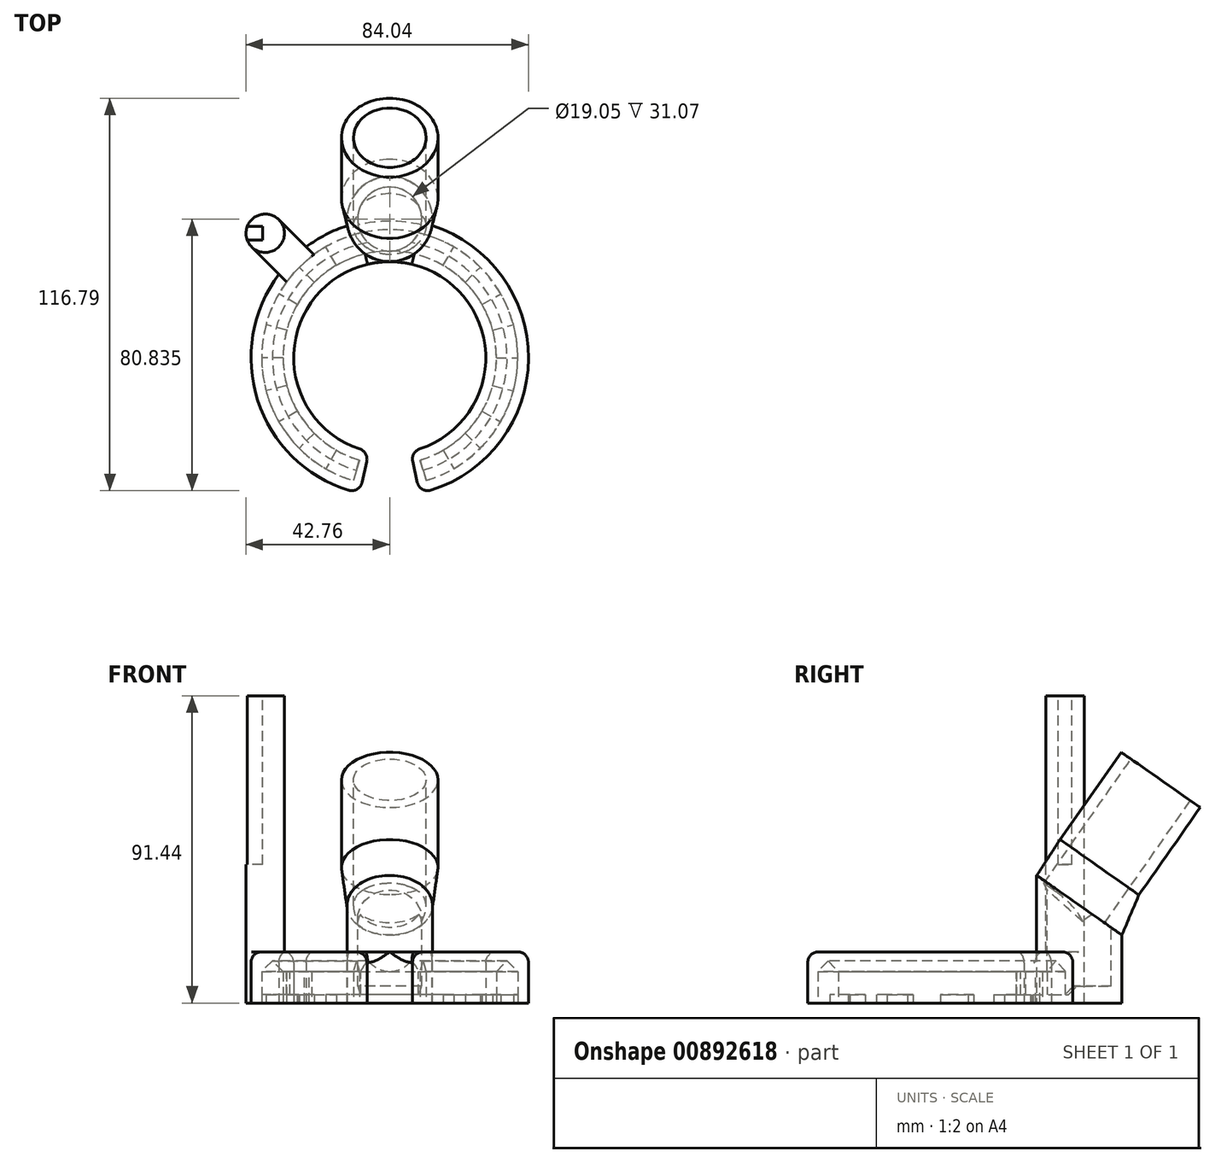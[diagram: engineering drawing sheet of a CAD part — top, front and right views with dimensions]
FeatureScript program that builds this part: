
annotation { "Feature Type Name" : "Feature", "Feature Type Description" : "" }
export const myFeature = defineFeature(function(context is Context, id is Id, definition is map)
    precondition{}
    {
        {
            var Q0;
            Q0=qCreatedBy(makeId("Top.planeOp"),FACE);
            var sketch = newSketch(context, id + "F0", { "sketchPlane" : qUnion([Q0])});
            skCircle(sketch, "E0", {"center": v(0, 0) * mm, "radius": 41.28 * mm});
            skCircle(sketch, "E1", {"center": v(0, 0) * mm, "radius": 28.58 * mm});
            skLineSegment(sketch, "E2", {"start": v(0, 0) * mm, "end": v(-10.13, -45.7) * mm});
            skLineSegment(sketch, "E3", {"start": v(0, 0) * mm, "end": v(10.1, -45.53) * mm});
            skLineSegment(sketch, "E4", {"start": v(0, 0) * mm, "end": v(0, -48.6) * mm});
            skLineSegment(sketch, "E5", {"start": v(0, 0) * mm, "end": v(-13.11, -44.27) * mm});
            skLineSegment(sketch, "E6", {"start": v(0, 0) * mm, "end": v(13.2, -44.55) * mm});
            skCircle(sketch, "E7", {"center": v(0, 0) * mm, "radius": 38.1 * mm, "construction": true});
            skCircle(sketch, "E8", {"center": v(0, 0) * mm, "radius": 31.75 * mm, "construction": true});
            skSolve(sketch);
        }
        {
            var Q0;
            {var subQ0=sQuery(id+"F0.wireOp",EDGE,"E5");var subQ1=sQuery(id+"F0.wireOp",EDGE,"E0");var subQ2=makeQuery(id+"F0.imprint","INTERSECT",VERTEX,{"derivedFrom":[subQ1,subQ0]});Q0=makeQuery(id+"F0.imprint","IMPRINT",FACE,{"disambiguationData":[TD([[makeQuery(id+"F0.imprint","IMPRINT",EDGE,{"disambiguationData":[TD([[subQ2,1.0]])],"derivedFrom":subQ1}),1.0]])]});}
            var Q1;
            {var subQ0=sQuery(id+"F0.wireOp",EDGE,"E5");var subQ1=sQuery(id+"F0.wireOp",EDGE,"E1");var subQ2=makeQuery(id+"F0.imprint","INTERSECT",VERTEX,{"derivedFrom":[subQ1,subQ0]});Q1=makeQuery(id+"F0.imprint","IMPRINT",FACE,{"disambiguationData":[TD([[makeQuery(id+"F0.imprint","IMPRINT",EDGE,{"disambiguationData":[TD([[subQ2,1.0]])],"derivedFrom":subQ1}),-1.0]])]});}
            extrude(context, id + "F1", {"entities" : qUnion([Q0, Q1]), "depth" : 15.24 * mm, "offsetDistance" : 25.4 * mm});
        }
        {
            var Q0;
            Q0=makeQuery(id+"F1.opExtrude","CAP_FACE",FACE,{"disambiguationData":[OSD([sQuery(id+"F0.wireOp",EDGE,"E0"),sQuery(id+"F0.wireOp",EDGE,"E1"),sQuery(id+"F0.wireOp",EDGE,"E5"),sQuery(id+"F0.wireOp",EDGE,"E6")])],"isStart":true});
            var sketch = newSketch(context, id + "F2", { "sketchPlane" : qUnion([Q0])});
            skCircle(sketch, "E9", {"center": v(0, 0) * mm, "radius": 38.1 * mm});
            skCircle(sketch, "E10", {"center": v(0, 0) * mm, "radius": 31.75 * mm});
            skLineSegment(sketch, "E11", {"start": v(0, 0) * mm, "end": v(0, 46.39) * mm});
            skLineSegment(sketch, "E12", {"start": v(0, 0) * mm, "end": v(-12.81, 47.82) * mm});
            skLineSegment(sketch, "E13", {"start": v(0, 0) * mm, "end": v(-48.58, 13.02) * mm});
            skLineSegment(sketch, "E14", {"start": v(0, 0) * mm, "end": v(-52.11, 0) * mm});
            skLineSegment(sketch, "E15", {"start": v(0, 0) * mm, "end": v(-46.55, -12.47) * mm});
            skLineSegment(sketch, "E16", {"start": v(0, 0) * mm, "end": v(-40.24, -23.23) * mm});
            skLineSegment(sketch, "E17", {"start": v(0, 0) * mm, "end": v(11.58, -43.2) * mm});
            skLineSegment(sketch, "E18", {"start": v(0, 0) * mm, "end": v(45.63, 0) * mm});
            skLineSegment(sketch, "E19", {"start": v(0, 0) * mm, "end": v(46.15, 12.37) * mm});
            skLineSegment(sketch, "E20", {"start": v(0, 0) * mm, "end": v(41.38, 23.89) * mm});
            skLineSegment(sketch, "E21", {"start": v(0, 0) * mm, "end": v(36.15, 36.15) * mm});
            skLineSegment(sketch, "E22", {"start": v(0, 0) * mm, "end": v(23.12, 40.04) * mm});
            skLineSegment(sketch, "E23", {"start": v(0, 0) * mm, "end": v(11.24, 41.94) * mm});
            skLineSegment(sketch, "E24", {"start": v(0, 0) * mm, "end": v(-24.22, 41.95) * mm});
            skLineSegment(sketch, "E25", {"start": v(0, 0) * mm, "end": v(-32.47, 32.47) * mm});
            skLineSegment(sketch, "E26", {"start": v(0, 0) * mm, "end": v(-45.6, 26.33) * mm});
            skLineSegment(sketch, "E27", {"start": v(0, 0) * mm, "end": v(-33.36, -33.36) * mm});
            skLineSegment(sketch, "E28", {"start": v(0, 0) * mm, "end": v(-22.54, -39.05) * mm});
            skLineSegment(sketch, "E29", {"start": v(0, 0) * mm, "end": v(-11.37, -42.45) * mm});
            skLineSegment(sketch, "E30", {"start": v(0, 0) * mm, "end": v(45.05, -12.07) * mm});
            skLineSegment(sketch, "E31", {"start": v(0, 0) * mm, "end": v(42.5, -24.54) * mm});
            skLineSegment(sketch, "E32", {"start": v(0, 0) * mm, "end": v(33.86, -33.86) * mm});
            skLineSegment(sketch, "E33", {"start": v(0, 0) * mm, "end": v(23.17, -40.14) * mm});
            skLineSegment(sketch, "E34", {"start": v(0, 0) * mm, "end": v(0, -46.71) * mm});
            skSolve(sketch);
        }
        {
            var Q0;
            {var subQ0=sQuery(id+"F2.wireOp",EDGE,"E24");var subQ1=sQuery(id+"F2.wireOp",EDGE,"E9");var subQ2=makeQuery(id+"F2.imprint","INTERSECT",VERTEX,{"derivedFrom":[subQ1,subQ0]});Q0=makeQuery(id+"F2.imprint","IMPRINT",FACE,{"disambiguationData":[TD([[makeQuery(id+"F2.imprint","IMPRINT",EDGE,{"disambiguationData":[TD([[subQ2,1.0]])],"derivedFrom":subQ1}),1.0]])]});}
            var Q1;
            {var subQ0=sQuery(id+"F2.wireOp",EDGE,"E25");var subQ1=sQuery(id+"F2.wireOp",EDGE,"E9");var subQ2=makeQuery(id+"F2.imprint","INTERSECT",VERTEX,{"derivedFrom":[subQ1,subQ0]});Q1=makeQuery(id+"F2.imprint","IMPRINT",FACE,{"disambiguationData":[TD([[makeQuery(id+"F2.imprint","IMPRINT",EDGE,{"disambiguationData":[TD([[subQ2,-1.0]])],"derivedFrom":subQ1}),1.0]])]});}
            var Q2;
            {var subQ0=sQuery(id+"F2.wireOp",EDGE,"E13");var subQ1=sQuery(id+"F2.wireOp",EDGE,"E9");var subQ2=makeQuery(id+"F2.imprint","INTERSECT",VERTEX,{"derivedFrom":[subQ1,subQ0]});Q2=makeQuery(id+"F2.imprint","IMPRINT",FACE,{"disambiguationData":[TD([[makeQuery(id+"F2.imprint","IMPRINT",EDGE,{"disambiguationData":[TD([[subQ2,-1.0]])],"derivedFrom":subQ1}),1.0]])]});}
            var Q3;
            {var subQ0=sQuery(id+"F2.wireOp",EDGE,"E15");var subQ1=sQuery(id+"F2.wireOp",EDGE,"E9");var subQ2=makeQuery(id+"F2.imprint","INTERSECT",VERTEX,{"derivedFrom":[subQ1,subQ0]});Q3=makeQuery(id+"F2.imprint","IMPRINT",FACE,{"disambiguationData":[TD([[makeQuery(id+"F2.imprint","IMPRINT",EDGE,{"disambiguationData":[TD([[subQ2,-1.0]])],"derivedFrom":subQ1}),1.0]])]});}
            var Q4;
            {var subQ0=sQuery(id+"F2.wireOp",EDGE,"E27");var subQ1=sQuery(id+"F2.wireOp",EDGE,"E9");var subQ2=makeQuery(id+"F2.imprint","INTERSECT",VERTEX,{"derivedFrom":[subQ1,subQ0]});Q4=makeQuery(id+"F2.imprint","IMPRINT",FACE,{"disambiguationData":[TD([[makeQuery(id+"F2.imprint","IMPRINT",EDGE,{"disambiguationData":[TD([[subQ2,-1.0]])],"derivedFrom":subQ1}),1.0]])]});}
            var Q5;
            {var subQ0=sQuery(id+"F2.wireOp",EDGE,"E22");var subQ1=sQuery(id+"F2.wireOp",EDGE,"E9");var subQ2=makeQuery(id+"F2.imprint","INTERSECT",VERTEX,{"derivedFrom":[subQ1,subQ0]});Q5=makeQuery(id+"F2.imprint","IMPRINT",FACE,{"disambiguationData":[TD([[makeQuery(id+"F2.imprint","IMPRINT",EDGE,{"disambiguationData":[TD([[subQ2,-1.0]])],"derivedFrom":subQ1}),1.0]])]});}
            var Q6;
            {var subQ0=sQuery(id+"F2.wireOp",EDGE,"E20");var subQ1=sQuery(id+"F2.wireOp",EDGE,"E9");var subQ2=makeQuery(id+"F2.imprint","INTERSECT",VERTEX,{"derivedFrom":[subQ1,subQ0]});Q6=makeQuery(id+"F2.imprint","IMPRINT",FACE,{"disambiguationData":[TD([[makeQuery(id+"F2.imprint","IMPRINT",EDGE,{"disambiguationData":[TD([[subQ2,-1.0]])],"derivedFrom":subQ1}),1.0]])]});}
            var Q7;
            {var subQ0=sQuery(id+"F2.wireOp",EDGE,"E19");var subQ1=sQuery(id+"F2.wireOp",EDGE,"E9");var subQ2=makeQuery(id+"F2.imprint","INTERSECT",VERTEX,{"derivedFrom":[subQ1,subQ0]});Q7=makeQuery(id+"F2.imprint","IMPRINT",FACE,{"disambiguationData":[TD([[makeQuery(id+"F2.imprint","IMPRINT",EDGE,{"disambiguationData":[TD([[subQ2,1.0]])],"derivedFrom":subQ1}),1.0]])]});}
            var Q8;
            {var subQ0=sQuery(id+"F2.wireOp",EDGE,"E31");var subQ1=sQuery(id+"F2.wireOp",EDGE,"E9");var subQ2=makeQuery(id+"F2.imprint","INTERSECT",VERTEX,{"derivedFrom":[subQ1,subQ0]});Q8=makeQuery(id+"F2.imprint","IMPRINT",FACE,{"disambiguationData":[TD([[makeQuery(id+"F2.imprint","IMPRINT",EDGE,{"disambiguationData":[TD([[subQ2,-1.0]])],"derivedFrom":subQ1}),1.0]])]});}
            var Q9;
            {var subQ0=sQuery(id+"F2.wireOp",EDGE,"E33");var subQ1=sQuery(id+"F2.wireOp",EDGE,"E9");var subQ2=makeQuery(id+"F2.imprint","INTERSECT",VERTEX,{"derivedFrom":[subQ1,subQ0]});Q9=makeQuery(id+"F2.imprint","IMPRINT",FACE,{"disambiguationData":[TD([[makeQuery(id+"F2.imprint","IMPRINT",EDGE,{"disambiguationData":[TD([[subQ2,-1.0]])],"derivedFrom":subQ1}),1.0]])]});}
            extrude(context, id + "F3", {"entities" : qUnion([Q0, Q1, Q2, Q3, Q4, Q5, Q6, Q7, Q8, Q9]), "operationType" : NewBodyOperationType.REMOVE, "oppositeDirection" : true, "depth" : 12.7 * mm, "offsetDistance" : 25.4 * mm});
        }
        {
            var Q0;
            Q0=makeQuery(id+"F1.opExtrude","SWEPT_FACE",FACE,{"disambiguationData":[OSD([sQuery(id+"F0.wireOp",EDGE,"E5")])]});
            var sketch = newSketch(context, id + "F4", { "sketchPlane" : qUnion([Q0])});
            skLineSegment(sketch, "E35.bottom", {"start": v(-31.75, 12.7) * mm, "end": v(-38.1, 12.7) * mm});
            skLineSegment(sketch, "E35.top", {"start": v(-31.75, 2.54) * mm, "end": v(-38.1, 2.54) * mm});
            skLineSegment(sketch, "E35.left", {"start": v(-31.75, 12.7) * mm, "end": v(-31.75, 2.54) * mm});
            skLineSegment(sketch, "E35.right", {"start": v(-38.1, 12.7) * mm, "end": v(-38.1, 2.54) * mm});
            skLineSegment(sketch, "E36", {"start": v(0, 0) * mm, "end": v(0, 28.6) * mm});
            skSolve(sketch);
        }
        {
            var Q0;
            Q0=makeQuery(id+"F4.imprint","IMPRINT",FACE,{"disambiguationData":[TD([[makeQuery(id+"F4.imprint","IMPRINT",EDGE,{"derivedFrom":sQuery(id+"F4.wireOp",EDGE,"E35.bottom")}),1.0]])]});
            var Q1;
            Q1=sQuery(id+"F4.wireOp",EDGE,"E36");
            revolve(context, id + "F5", {"operationType" : NewBodyOperationType.REMOVE, "surfaceOperationType" : NewSurfaceOperationType.NEW, "entities" : qUnion([Q0]), "axis" : qUnion([Q1]), "revolveType" : RevolveType.FULL, "oppositeDirection" : true});
        }
        {
            var Q0;
            {var subQ0=sQuery(id+"F0.wireOp",EDGE,"E2");var subQ1=sQuery(id+"F0.wireOp",EDGE,"E0");var subQ2=makeQuery(id+"F0.imprint","INTERSECT",VERTEX,{"derivedFrom":[subQ1,subQ0]});Q0=makeQuery(id+"F0.imprint","IMPRINT",FACE,{"disambiguationData":[TD([[makeQuery(id+"F0.imprint","IMPRINT",EDGE,{"disambiguationData":[TD([[subQ2,1.0]])],"derivedFrom":subQ1}),1.0]])]});}
            var Q1;
            {var subQ0=sQuery(id+"F0.wireOp",EDGE,"E3");var subQ1=sQuery(id+"F0.wireOp",EDGE,"E0");var subQ2=makeQuery(id+"F0.imprint","INTERSECT",VERTEX,{"derivedFrom":[subQ1,subQ0]});Q1=makeQuery(id+"F0.imprint","IMPRINT",FACE,{"disambiguationData":[TD([[makeQuery(id+"F0.imprint","IMPRINT",EDGE,{"disambiguationData":[TD([[subQ2,-1.0]])],"derivedFrom":subQ1}),1.0]])]});}
            extrude(context, id + "F6", {"entities" : qUnion([Q0, Q1]), "operationType" : NewBodyOperationType.ADD, "depth" : 15.24 * mm, "offsetDistance" : 25.4 * mm});
        }
        {
            var Q0;
            {var subQ0=sQuery(id+"F2.wireOp",EDGE,"E10");Q0=makeQuery(id+"F5.boolean.opBoolean","MERGE",EDGE,{"derivedFrom":[makeQuery(id+"F3.boolean.opBoolean","COPY",EDGE,{"derivedFrom":makeQuery(id+"F3.opExtrude","CAP_EDGE",EDGE,{"disambiguationData":[OSD([subQ0]),TDD([makeQuery(id+"F2.imprint","IMPRINT",EDGE,{"disambiguationData":[TD([[makeQuery(id+"F2.imprint","INTERSECT",VERTEX,{"derivedFrom":[subQ0,sQuery(id+"F2.wireOp",EDGE,"E19")]}),1.0]])],"derivedFrom":subQ0})])],"isStart":false})}),makeQuery(id+"F3.boolean.opBoolean","COPY",EDGE,{"derivedFrom":makeQuery(id+"F3.opExtrude","CAP_EDGE",EDGE,{"disambiguationData":[OSD([subQ0]),TDD([makeQuery(id+"F2.imprint","IMPRINT",EDGE,{"disambiguationData":[TD([[makeQuery(id+"F2.imprint","INTERSECT",VERTEX,{"derivedFrom":[subQ0,sQuery(id+"F2.wireOp",EDGE,"E20")]}),-1.0]])],"derivedFrom":subQ0})])],"isStart":false})}),makeQuery(id+"F3.boolean.opBoolean","COPY",EDGE,{"derivedFrom":makeQuery(id+"F3.opExtrude","CAP_EDGE",EDGE,{"disambiguationData":[OSD([subQ0]),TDD([makeQuery(id+"F2.imprint","IMPRINT",EDGE,{"disambiguationData":[TD([[makeQuery(id+"F2.imprint","INTERSECT",VERTEX,{"derivedFrom":[subQ0,sQuery(id+"F2.wireOp",EDGE,"E22")]}),-1.0]])],"derivedFrom":subQ0})])],"isStart":false})}),makeQuery(id+"F3.boolean.opBoolean","COPY",EDGE,{"derivedFrom":makeQuery(id+"F3.opExtrude","CAP_EDGE",EDGE,{"disambiguationData":[OSD([subQ0]),TDD([makeQuery(id+"F2.imprint","IMPRINT",EDGE,{"disambiguationData":[TD([[makeQuery(id+"F2.imprint","INTERSECT",VERTEX,{"derivedFrom":[subQ0,sQuery(id+"F2.wireOp",EDGE,"E24")]}),1.0]])],"derivedFrom":subQ0})])],"isStart":false})}),makeQuery(id+"F3.boolean.opBoolean","COPY",EDGE,{"derivedFrom":makeQuery(id+"F3.opExtrude","CAP_EDGE",EDGE,{"disambiguationData":[OSD([subQ0]),TDD([makeQuery(id+"F2.imprint","IMPRINT",EDGE,{"disambiguationData":[TD([[makeQuery(id+"F2.imprint","INTERSECT",VERTEX,{"derivedFrom":[subQ0,sQuery(id+"F2.wireOp",EDGE,"E25")]}),-1.0]])],"derivedFrom":subQ0})])],"isStart":false})}),makeQuery(id+"F3.boolean.opBoolean","COPY",EDGE,{"derivedFrom":makeQuery(id+"F3.opExtrude","CAP_EDGE",EDGE,{"disambiguationData":[OSD([subQ0]),TDD([makeQuery(id+"F2.imprint","IMPRINT",EDGE,{"disambiguationData":[TD([[makeQuery(id+"F2.imprint","INTERSECT",VERTEX,{"derivedFrom":[subQ0,sQuery(id+"F2.wireOp",EDGE,"E13")]}),-1.0]])],"derivedFrom":subQ0})])],"isStart":false})}),makeQuery(id+"F3.boolean.opBoolean","COPY",EDGE,{"derivedFrom":makeQuery(id+"F3.opExtrude","CAP_EDGE",EDGE,{"disambiguationData":[OSD([subQ0]),TDD([makeQuery(id+"F2.imprint","IMPRINT",EDGE,{"disambiguationData":[TD([[makeQuery(id+"F2.imprint","INTERSECT",VERTEX,{"derivedFrom":[subQ0,sQuery(id+"F2.wireOp",EDGE,"E15")]}),-1.0]])],"derivedFrom":subQ0})])],"isStart":false})}),makeQuery(id+"F3.boolean.opBoolean","COPY",EDGE,{"derivedFrom":makeQuery(id+"F3.opExtrude","CAP_EDGE",EDGE,{"disambiguationData":[OSD([subQ0]),TDD([makeQuery(id+"F2.imprint","IMPRINT",EDGE,{"disambiguationData":[TD([[makeQuery(id+"F2.imprint","INTERSECT",VERTEX,{"derivedFrom":[subQ0,sQuery(id+"F2.wireOp",EDGE,"E27")]}),-1.0]])],"derivedFrom":subQ0})])],"isStart":false})}),makeQuery(id+"F3.boolean.opBoolean","COPY",EDGE,{"derivedFrom":makeQuery(id+"F3.opExtrude","CAP_EDGE",EDGE,{"disambiguationData":[OSD([subQ0]),TDD([makeQuery(id+"F2.imprint","IMPRINT",EDGE,{"disambiguationData":[TD([[makeQuery(id+"F2.imprint","INTERSECT",VERTEX,{"derivedFrom":[subQ0,sQuery(id+"F2.wireOp",EDGE,"E29")]}),-1.0]])],"derivedFrom":subQ0})])],"isStart":false})}),makeQuery(id+"F3.boolean.opBoolean","COPY",EDGE,{"derivedFrom":makeQuery(id+"F3.opExtrude","CAP_EDGE",EDGE,{"disambiguationData":[OSD([subQ0]),TDD([makeQuery(id+"F2.imprint","IMPRINT",EDGE,{"disambiguationData":[TD([[makeQuery(id+"F2.imprint","INTERSECT",VERTEX,{"derivedFrom":[subQ0,sQuery(id+"F2.wireOp",EDGE,"E33")]}),-1.0]])],"derivedFrom":subQ0})])],"isStart":false})}),makeQuery(id+"F3.boolean.opBoolean","COPY",EDGE,{"derivedFrom":makeQuery(id+"F3.opExtrude","CAP_EDGE",EDGE,{"disambiguationData":[OSD([subQ0]),TDD([makeQuery(id+"F2.imprint","IMPRINT",EDGE,{"disambiguationData":[TD([[makeQuery(id+"F2.imprint","INTERSECT",VERTEX,{"derivedFrom":[subQ0,sQuery(id+"F2.wireOp",EDGE,"E31")]}),-1.0]])],"derivedFrom":subQ0})])],"isStart":false})})],"fromTools":[makeQuery(id+"F5.opRevolve","SWEPT_EDGE",EDGE,{"disambiguationData":[OSD([sQuery(id+"F4.wireOp",EDGE,"E35.bottom"),sQuery(id+"F4.wireOp",EDGE,"E35.left")])]})]});}
            var Q1;
            {var subQ0=sQuery(id+"F2.wireOp",EDGE,"E9");Q1=makeQuery(id+"F5.boolean.opBoolean","MERGE",EDGE,{"derivedFrom":[makeQuery(id+"F3.boolean.opBoolean","COPY",EDGE,{"derivedFrom":makeQuery(id+"F3.opExtrude","CAP_EDGE",EDGE,{"disambiguationData":[OSD([subQ0]),TDD([makeQuery(id+"F2.imprint","IMPRINT",EDGE,{"disambiguationData":[TD([[makeQuery(id+"F2.imprint","INTERSECT",VERTEX,{"derivedFrom":[subQ0,sQuery(id+"F2.wireOp",EDGE,"E19")]}),1.0]])],"derivedFrom":subQ0})])],"isStart":false})}),makeQuery(id+"F3.boolean.opBoolean","COPY",EDGE,{"derivedFrom":makeQuery(id+"F3.opExtrude","CAP_EDGE",EDGE,{"disambiguationData":[OSD([subQ0]),TDD([makeQuery(id+"F2.imprint","IMPRINT",EDGE,{"disambiguationData":[TD([[makeQuery(id+"F2.imprint","INTERSECT",VERTEX,{"derivedFrom":[subQ0,sQuery(id+"F2.wireOp",EDGE,"E20")]}),-1.0]])],"derivedFrom":subQ0})])],"isStart":false})}),makeQuery(id+"F3.boolean.opBoolean","COPY",EDGE,{"derivedFrom":makeQuery(id+"F3.opExtrude","CAP_EDGE",EDGE,{"disambiguationData":[OSD([subQ0]),TDD([makeQuery(id+"F2.imprint","IMPRINT",EDGE,{"disambiguationData":[TD([[makeQuery(id+"F2.imprint","INTERSECT",VERTEX,{"derivedFrom":[subQ0,sQuery(id+"F2.wireOp",EDGE,"E22")]}),-1.0]])],"derivedFrom":subQ0})])],"isStart":false})}),makeQuery(id+"F3.boolean.opBoolean","COPY",EDGE,{"derivedFrom":makeQuery(id+"F3.opExtrude","CAP_EDGE",EDGE,{"disambiguationData":[OSD([subQ0]),TDD([makeQuery(id+"F2.imprint","IMPRINT",EDGE,{"disambiguationData":[TD([[makeQuery(id+"F2.imprint","INTERSECT",VERTEX,{"derivedFrom":[subQ0,sQuery(id+"F2.wireOp",EDGE,"E24")]}),1.0]])],"derivedFrom":subQ0})])],"isStart":false})}),makeQuery(id+"F3.boolean.opBoolean","COPY",EDGE,{"derivedFrom":makeQuery(id+"F3.opExtrude","CAP_EDGE",EDGE,{"disambiguationData":[OSD([subQ0]),TDD([makeQuery(id+"F2.imprint","IMPRINT",EDGE,{"disambiguationData":[TD([[makeQuery(id+"F2.imprint","INTERSECT",VERTEX,{"derivedFrom":[subQ0,sQuery(id+"F2.wireOp",EDGE,"E25")]}),-1.0]])],"derivedFrom":subQ0})])],"isStart":false})}),makeQuery(id+"F3.boolean.opBoolean","COPY",EDGE,{"derivedFrom":makeQuery(id+"F3.opExtrude","CAP_EDGE",EDGE,{"disambiguationData":[OSD([subQ0]),TDD([makeQuery(id+"F2.imprint","IMPRINT",EDGE,{"disambiguationData":[TD([[makeQuery(id+"F2.imprint","INTERSECT",VERTEX,{"derivedFrom":[subQ0,sQuery(id+"F2.wireOp",EDGE,"E13")]}),-1.0]])],"derivedFrom":subQ0})])],"isStart":false})}),makeQuery(id+"F3.boolean.opBoolean","COPY",EDGE,{"derivedFrom":makeQuery(id+"F3.opExtrude","CAP_EDGE",EDGE,{"disambiguationData":[OSD([subQ0]),TDD([makeQuery(id+"F2.imprint","IMPRINT",EDGE,{"disambiguationData":[TD([[makeQuery(id+"F2.imprint","INTERSECT",VERTEX,{"derivedFrom":[subQ0,sQuery(id+"F2.wireOp",EDGE,"E15")]}),-1.0]])],"derivedFrom":subQ0})])],"isStart":false})}),makeQuery(id+"F3.boolean.opBoolean","COPY",EDGE,{"derivedFrom":makeQuery(id+"F3.opExtrude","CAP_EDGE",EDGE,{"disambiguationData":[OSD([subQ0]),TDD([makeQuery(id+"F2.imprint","IMPRINT",EDGE,{"disambiguationData":[TD([[makeQuery(id+"F2.imprint","INTERSECT",VERTEX,{"derivedFrom":[subQ0,sQuery(id+"F2.wireOp",EDGE,"E27")]}),-1.0]])],"derivedFrom":subQ0})])],"isStart":false})}),makeQuery(id+"F3.boolean.opBoolean","COPY",EDGE,{"derivedFrom":makeQuery(id+"F3.opExtrude","CAP_EDGE",EDGE,{"disambiguationData":[OSD([subQ0]),TDD([makeQuery(id+"F2.imprint","IMPRINT",EDGE,{"disambiguationData":[TD([[makeQuery(id+"F2.imprint","INTERSECT",VERTEX,{"derivedFrom":[subQ0,sQuery(id+"F2.wireOp",EDGE,"E29")]}),-1.0]])],"derivedFrom":subQ0})])],"isStart":false})}),makeQuery(id+"F3.boolean.opBoolean","COPY",EDGE,{"derivedFrom":makeQuery(id+"F3.opExtrude","CAP_EDGE",EDGE,{"disambiguationData":[OSD([subQ0]),TDD([makeQuery(id+"F2.imprint","IMPRINT",EDGE,{"disambiguationData":[TD([[makeQuery(id+"F2.imprint","INTERSECT",VERTEX,{"derivedFrom":[subQ0,sQuery(id+"F2.wireOp",EDGE,"E33")]}),-1.0]])],"derivedFrom":subQ0})])],"isStart":false})}),makeQuery(id+"F3.boolean.opBoolean","COPY",EDGE,{"derivedFrom":makeQuery(id+"F3.opExtrude","CAP_EDGE",EDGE,{"disambiguationData":[OSD([subQ0]),TDD([makeQuery(id+"F2.imprint","IMPRINT",EDGE,{"disambiguationData":[TD([[makeQuery(id+"F2.imprint","INTERSECT",VERTEX,{"derivedFrom":[subQ0,sQuery(id+"F2.wireOp",EDGE,"E31")]}),-1.0]])],"derivedFrom":subQ0})])],"isStart":false})})],"fromTools":[makeQuery(id+"F5.opRevolve","SWEPT_EDGE",EDGE,{"disambiguationData":[OSD([sQuery(id+"F4.wireOp",EDGE,"E35.bottom"),sQuery(id+"F4.wireOp",EDGE,"E35.right")])]})]});}
            chamfer(context, id + "F7", {"entities" : qUnion([Q0, Q1]), "width" : 3.3 * mm, "tangentPropagation" : true});
        }
        {
            var Q0;
            {var subQ0=sQuery(id+"F0.wireOp",EDGE,"E6");var subQ1=sQuery(id+"F0.wireOp",EDGE,"E1");var subQ2=sQuery(id+"F0.wireOp",EDGE,"E0");var subQ3=sQuery(id+"F0.wireOp",EDGE,"E5");Q0=makeQuery(id+"F6.boolean.opBoolean","MERGE",FACE,{"derivedFrom":[makeQuery(id+"F1.opExtrude","CAP_FACE",FACE,{"disambiguationData":[OSD([subQ2,subQ1,subQ3,subQ0])],"isStart":false}),makeQuery(id+"F6.opExtrude","CAP_FACE",FACE,{"disambiguationData":[OSD([subQ2,subQ1,sQuery(id+"F0.wireOp",EDGE,"E2"),subQ3])],"isStart":false}),makeQuery(id+"F6.opExtrude","CAP_FACE",FACE,{"disambiguationData":[OSD([subQ2,subQ1,sQuery(id+"F0.wireOp",EDGE,"E3"),subQ0])],"isStart":false})]});}
            var sketch = newSketch(context, id + "F8", { "sketchPlane" : qUnion([Q0])});
            skCircle(sketch, "E37", {"center": v(0, 41.28) * mm, "radius": 12.7 * mm});
            skCircle(sketch, "E38", {"center": v(0, 41.28) * mm, "radius": 9.53 * mm});
            skSolve(sketch);
        }
        {
            var Q0;
            {var subQ0=sQuery(id+"F8.wireOp",EDGE,"E37");var subQ1=sQuery(id+"F0.wireOp",EDGE,"E0");var subQ2=makeQuery(id+"F6.boolean.opBoolean","MERGE",EDGE,{"derivedFrom":[makeQuery(id+"F1.opExtrude","CAP_EDGE",EDGE,{"disambiguationData":[OSD([subQ1])],"isStart":false}),makeQuery(id+"F6.opExtrude","CAP_EDGE",EDGE,{"disambiguationData":[OSD([subQ1]),TDD([makeQuery(id+"F0.imprint","IMPRINT",EDGE,{"disambiguationData":[TD([[makeQuery(id+"F0.imprint","INTERSECT",VERTEX,{"derivedFrom":[subQ1,sQuery(id+"F0.wireOp",EDGE,"E2")]}),1.0]])],"derivedFrom":subQ1})])],"isStart":false}),makeQuery(id+"F6.opExtrude","CAP_EDGE",EDGE,{"disambiguationData":[OSD([subQ1]),TDD([makeQuery(id+"F0.imprint","IMPRINT",EDGE,{"disambiguationData":[TD([[makeQuery(id+"F0.imprint","INTERSECT",VERTEX,{"derivedFrom":[subQ1,sQuery(id+"F0.wireOp",EDGE,"E3")]}),-1.0]])],"derivedFrom":subQ1})])],"isStart":false})]});var subQ3=makeQuery(id+"F8.imprint","INTERSECT",VERTEX,{"disambiguationData":[OD(0.0)],"derivedFrom":[subQ2,subQ0]});Q0=makeQuery(id+"F8.imprint","IMPRINT",FACE,{"disambiguationData":[TD([[makeQuery(id+"F8.imprint","IMPRINT",EDGE,{"disambiguationData":[TD([[subQ3,1.0]])],"derivedFrom":subQ0}),1.0]])]});}
            extrude(context, id + "F9", {"entities" : qUnion([Q0]), "operationType" : NewBodyOperationType.ADD, "oppositeDirection" : true, "depth" : 15.24 * mm, "offsetDistance" : 25.4 * mm});
        }
        {
            var Q0;
            {var subQ1=sQuery(id+"F0.wireOp",EDGE,"E3");var subQ4=sQuery(id+"F0.wireOp",EDGE,"E2");var subQ9=sQuery(id+"F8.wireOp",EDGE,"E37");var subQ11=sQuery(id+"F0.wireOp",EDGE,"E1");var subQ12=makeQuery(id+"F8.imprint","INTERSECT",VERTEX,{"derivedFrom":[makeQuery(id+"F6.boolean.opBoolean","MERGE",EDGE,{"derivedFrom":[makeQuery(id+"F1.opExtrude","CAP_EDGE",EDGE,{"disambiguationData":[OSD([subQ11])],"isStart":false}),makeQuery(id+"F6.opExtrude","CAP_EDGE",EDGE,{"disambiguationData":[OSD([subQ11]),TDD([makeQuery(id+"F0.imprint","IMPRINT",EDGE,{"disambiguationData":[TD([[makeQuery(id+"F0.imprint","INTERSECT",VERTEX,{"derivedFrom":[subQ11,subQ4]}),1.0]])],"derivedFrom":subQ11})])],"isStart":false}),makeQuery(id+"F6.opExtrude","CAP_EDGE",EDGE,{"disambiguationData":[OSD([subQ11]),TDD([makeQuery(id+"F0.imprint","IMPRINT",EDGE,{"disambiguationData":[TD([[makeQuery(id+"F0.imprint","INTERSECT",VERTEX,{"derivedFrom":[subQ11,subQ1]}),-1.0]])],"derivedFrom":subQ11})])],"isStart":false})]}),subQ9]});Q0=makeQuery(id+"F8.imprint","IMPRINT",FACE,{"disambiguationData":[TD([[makeQuery(id+"F8.imprint","IMPRINT",EDGE,{"disambiguationData":[TD([[subQ12,1.0]])],"derivedFrom":subQ9}),1.0]])]});}
            var Q1;
            {var subQ0=sQuery(id+"F8.wireOp",EDGE,"E37");var subQ1=sQuery(id+"F0.wireOp",EDGE,"E0");var subQ2=makeQuery(id+"F6.boolean.opBoolean","MERGE",EDGE,{"derivedFrom":[makeQuery(id+"F1.opExtrude","CAP_EDGE",EDGE,{"disambiguationData":[OSD([subQ1])],"isStart":false}),makeQuery(id+"F6.opExtrude","CAP_EDGE",EDGE,{"disambiguationData":[OSD([subQ1]),TDD([makeQuery(id+"F0.imprint","IMPRINT",EDGE,{"disambiguationData":[TD([[makeQuery(id+"F0.imprint","INTERSECT",VERTEX,{"derivedFrom":[subQ1,sQuery(id+"F0.wireOp",EDGE,"E2")]}),1.0]])],"derivedFrom":subQ1})])],"isStart":false}),makeQuery(id+"F6.opExtrude","CAP_EDGE",EDGE,{"disambiguationData":[OSD([subQ1]),TDD([makeQuery(id+"F0.imprint","IMPRINT",EDGE,{"disambiguationData":[TD([[makeQuery(id+"F0.imprint","INTERSECT",VERTEX,{"derivedFrom":[subQ1,sQuery(id+"F0.wireOp",EDGE,"E3")]}),-1.0]])],"derivedFrom":subQ1})])],"isStart":false})]});var subQ3=makeQuery(id+"F8.imprint","INTERSECT",VERTEX,{"disambiguationData":[OD(0.0)],"derivedFrom":[subQ2,subQ0]});Q1=makeQuery(id+"F8.imprint","IMPRINT",FACE,{"disambiguationData":[TD([[makeQuery(id+"F8.imprint","IMPRINT",EDGE,{"disambiguationData":[TD([[subQ3,1.0]])],"derivedFrom":subQ0}),1.0]])]});}
            extrude(context, id + "F10", {"entities" : qUnion([Q0, Q1]), "operationType" : NewBodyOperationType.ADD, "depth" : 25.4 * mm, "offsetDistance" : 25.4 * mm});
        }
        {
            var Q0;
            {var subQ0=sQuery(id+"F8.wireOp",EDGE,"E38");var subQ1=sQuery(id+"F0.wireOp",EDGE,"E0");var subQ2=makeQuery(id+"F6.boolean.opBoolean","MERGE",EDGE,{"derivedFrom":[makeQuery(id+"F1.opExtrude","CAP_EDGE",EDGE,{"disambiguationData":[OSD([subQ1])],"isStart":false}),makeQuery(id+"F6.opExtrude","CAP_EDGE",EDGE,{"disambiguationData":[OSD([subQ1]),TDD([makeQuery(id+"F0.imprint","IMPRINT",EDGE,{"disambiguationData":[TD([[makeQuery(id+"F0.imprint","INTERSECT",VERTEX,{"derivedFrom":[subQ1,sQuery(id+"F0.wireOp",EDGE,"E2")]}),1.0]])],"derivedFrom":subQ1})])],"isStart":false}),makeQuery(id+"F6.opExtrude","CAP_EDGE",EDGE,{"disambiguationData":[OSD([subQ1]),TDD([makeQuery(id+"F0.imprint","IMPRINT",EDGE,{"disambiguationData":[TD([[makeQuery(id+"F0.imprint","INTERSECT",VERTEX,{"derivedFrom":[subQ1,sQuery(id+"F0.wireOp",EDGE,"E3")]}),-1.0]])],"derivedFrom":subQ1})])],"isStart":false})]});var subQ3=makeQuery(id+"F8.imprint","INTERSECT",VERTEX,{"disambiguationData":[OD(0.0)],"derivedFrom":[subQ2,subQ0]});Q0=makeQuery(id+"F8.imprint","IMPRINT",FACE,{"disambiguationData":[TD([[makeQuery(id+"F8.imprint","IMPRINT",EDGE,{"disambiguationData":[TD([[subQ3,1.0]])],"derivedFrom":subQ0}),1.0]])]});}
            extrude(context, id + "F11", {"entities" : qUnion([Q0]), "operationType" : NewBodyOperationType.ADD, "oppositeDirection" : true, "depth" : 15.24 * mm, "offsetDistance" : 25.4 * mm});
        }
        {
            var Q0;
            {var subQ0=sQuery(id+"F8.wireOp",EDGE,"E38");var subQ1=sQuery(id+"F0.wireOp",EDGE,"E0");var subQ2=makeQuery(id+"F6.boolean.opBoolean","MERGE",EDGE,{"derivedFrom":[makeQuery(id+"F1.opExtrude","CAP_EDGE",EDGE,{"disambiguationData":[OSD([subQ1])],"isStart":false}),makeQuery(id+"F6.opExtrude","CAP_EDGE",EDGE,{"disambiguationData":[OSD([subQ1]),TDD([makeQuery(id+"F0.imprint","IMPRINT",EDGE,{"disambiguationData":[TD([[makeQuery(id+"F0.imprint","INTERSECT",VERTEX,{"derivedFrom":[subQ1,sQuery(id+"F0.wireOp",EDGE,"E2")]}),1.0]])],"derivedFrom":subQ1})])],"isStart":false}),makeQuery(id+"F6.opExtrude","CAP_EDGE",EDGE,{"disambiguationData":[OSD([subQ1]),TDD([makeQuery(id+"F0.imprint","IMPRINT",EDGE,{"disambiguationData":[TD([[makeQuery(id+"F0.imprint","INTERSECT",VERTEX,{"derivedFrom":[subQ1,sQuery(id+"F0.wireOp",EDGE,"E3")]}),-1.0]])],"derivedFrom":subQ1})])],"isStart":false})]});var subQ3=makeQuery(id+"F8.imprint","INTERSECT",VERTEX,{"disambiguationData":[OD(0.0)],"derivedFrom":[subQ2,subQ0]});Q0=makeQuery(id+"F8.imprint","IMPRINT",FACE,{"disambiguationData":[TD([[makeQuery(id+"F8.imprint","IMPRINT",EDGE,{"disambiguationData":[TD([[subQ3,1.0]])],"derivedFrom":subQ0}),1.0]])]});}
            var Q1;
            {var subQ0=sQuery(id+"F8.wireOp",EDGE,"E38");var subQ1=sQuery(id+"F0.wireOp",EDGE,"E0");var subQ2=makeQuery(id+"F6.boolean.opBoolean","MERGE",EDGE,{"derivedFrom":[makeQuery(id+"F1.opExtrude","CAP_EDGE",EDGE,{"disambiguationData":[OSD([subQ1])],"isStart":false}),makeQuery(id+"F6.opExtrude","CAP_EDGE",EDGE,{"disambiguationData":[OSD([subQ1]),TDD([makeQuery(id+"F0.imprint","IMPRINT",EDGE,{"disambiguationData":[TD([[makeQuery(id+"F0.imprint","INTERSECT",VERTEX,{"derivedFrom":[subQ1,sQuery(id+"F0.wireOp",EDGE,"E2")]}),1.0]])],"derivedFrom":subQ1})])],"isStart":false}),makeQuery(id+"F6.opExtrude","CAP_EDGE",EDGE,{"disambiguationData":[OSD([subQ1]),TDD([makeQuery(id+"F0.imprint","IMPRINT",EDGE,{"disambiguationData":[TD([[makeQuery(id+"F0.imprint","INTERSECT",VERTEX,{"derivedFrom":[subQ1,sQuery(id+"F0.wireOp",EDGE,"E3")]}),-1.0]])],"derivedFrom":subQ1})])],"isStart":false})]});var subQ3=makeQuery(id+"F8.imprint","INTERSECT",VERTEX,{"disambiguationData":[OD(0.0)],"derivedFrom":[subQ2,subQ0]});Q1=makeQuery(id+"F8.imprint","IMPRINT",FACE,{"disambiguationData":[TD([[makeQuery(id+"F8.imprint","IMPRINT",EDGE,{"disambiguationData":[TD([[subQ3,-1.0]])],"derivedFrom":subQ0}),1.0]])]});}
            extrude(context, id + "F12", {"entities" : qUnion([Q0, Q1]), "operationType" : NewBodyOperationType.REMOVE, "oppositeDirection" : true, "depth" : 10.16 * mm, "offsetDistance" : 25.4 * mm});
        }
        {
            var Q0;
            {var subQ0=sQuery(id+"F2.wireOp",EDGE,"E9");Q0=makeQuery(id+"F12.boolean.opBoolean","INTERSECT",EDGE,{"derivedFrom":[makeQuery(id+"F5.boolean.opBoolean","MERGE",FACE,{"derivedFrom":[makeQuery(id+"F3.boolean.opBoolean","COPY",FACE,{"derivedFrom":makeQuery(id+"F3.opExtrude","SWEPT_FACE",FACE,{"disambiguationData":[OSD([subQ0]),TDD([makeQuery(id+"F2.imprint","IMPRINT",EDGE,{"disambiguationData":[TD([[makeQuery(id+"F2.imprint","INTERSECT",VERTEX,{"derivedFrom":[subQ0,sQuery(id+"F2.wireOp",EDGE,"E19")]}),1.0]])],"derivedFrom":subQ0})])]})}),makeQuery(id+"F3.boolean.opBoolean","COPY",FACE,{"derivedFrom":makeQuery(id+"F3.opExtrude","SWEPT_FACE",FACE,{"disambiguationData":[OSD([subQ0]),TDD([makeQuery(id+"F2.imprint","IMPRINT",EDGE,{"disambiguationData":[TD([[makeQuery(id+"F2.imprint","INTERSECT",VERTEX,{"derivedFrom":[subQ0,sQuery(id+"F2.wireOp",EDGE,"E20")]}),-1.0]])],"derivedFrom":subQ0})])]})}),makeQuery(id+"F3.boolean.opBoolean","COPY",FACE,{"derivedFrom":makeQuery(id+"F3.opExtrude","SWEPT_FACE",FACE,{"disambiguationData":[OSD([subQ0]),TDD([makeQuery(id+"F2.imprint","IMPRINT",EDGE,{"disambiguationData":[TD([[makeQuery(id+"F2.imprint","INTERSECT",VERTEX,{"derivedFrom":[subQ0,sQuery(id+"F2.wireOp",EDGE,"E22")]}),-1.0]])],"derivedFrom":subQ0})])]})}),makeQuery(id+"F3.boolean.opBoolean","COPY",FACE,{"derivedFrom":makeQuery(id+"F3.opExtrude","SWEPT_FACE",FACE,{"disambiguationData":[OSD([subQ0]),TDD([makeQuery(id+"F2.imprint","IMPRINT",EDGE,{"disambiguationData":[TD([[makeQuery(id+"F2.imprint","INTERSECT",VERTEX,{"derivedFrom":[subQ0,sQuery(id+"F2.wireOp",EDGE,"E24")]}),1.0]])],"derivedFrom":subQ0})])]})}),makeQuery(id+"F3.boolean.opBoolean","COPY",FACE,{"derivedFrom":makeQuery(id+"F3.opExtrude","SWEPT_FACE",FACE,{"disambiguationData":[OSD([subQ0]),TDD([makeQuery(id+"F2.imprint","IMPRINT",EDGE,{"disambiguationData":[TD([[makeQuery(id+"F2.imprint","INTERSECT",VERTEX,{"derivedFrom":[subQ0,sQuery(id+"F2.wireOp",EDGE,"E25")]}),-1.0]])],"derivedFrom":subQ0})])]})}),makeQuery(id+"F3.boolean.opBoolean","COPY",FACE,{"derivedFrom":makeQuery(id+"F3.opExtrude","SWEPT_FACE",FACE,{"disambiguationData":[OSD([subQ0]),TDD([makeQuery(id+"F2.imprint","IMPRINT",EDGE,{"disambiguationData":[TD([[makeQuery(id+"F2.imprint","INTERSECT",VERTEX,{"derivedFrom":[subQ0,sQuery(id+"F2.wireOp",EDGE,"E13")]}),-1.0]])],"derivedFrom":subQ0})])]})}),makeQuery(id+"F3.boolean.opBoolean","COPY",FACE,{"derivedFrom":makeQuery(id+"F3.opExtrude","SWEPT_FACE",FACE,{"disambiguationData":[OSD([subQ0]),TDD([makeQuery(id+"F2.imprint","IMPRINT",EDGE,{"disambiguationData":[TD([[makeQuery(id+"F2.imprint","INTERSECT",VERTEX,{"derivedFrom":[subQ0,sQuery(id+"F2.wireOp",EDGE,"E15")]}),-1.0]])],"derivedFrom":subQ0})])]})}),makeQuery(id+"F3.boolean.opBoolean","COPY",FACE,{"derivedFrom":makeQuery(id+"F3.opExtrude","SWEPT_FACE",FACE,{"disambiguationData":[OSD([subQ0]),TDD([makeQuery(id+"F2.imprint","IMPRINT",EDGE,{"disambiguationData":[TD([[makeQuery(id+"F2.imprint","INTERSECT",VERTEX,{"derivedFrom":[subQ0,sQuery(id+"F2.wireOp",EDGE,"E27")]}),-1.0]])],"derivedFrom":subQ0})])]})}),makeQuery(id+"F3.boolean.opBoolean","COPY",FACE,{"derivedFrom":makeQuery(id+"F3.opExtrude","SWEPT_FACE",FACE,{"disambiguationData":[OSD([subQ0]),TDD([makeQuery(id+"F2.imprint","IMPRINT",EDGE,{"disambiguationData":[TD([[makeQuery(id+"F2.imprint","INTERSECT",VERTEX,{"derivedFrom":[subQ0,sQuery(id+"F2.wireOp",EDGE,"E33")]}),-1.0]])],"derivedFrom":subQ0})])]})}),makeQuery(id+"F3.boolean.opBoolean","COPY",FACE,{"derivedFrom":makeQuery(id+"F3.opExtrude","SWEPT_FACE",FACE,{"disambiguationData":[OSD([subQ0]),TDD([makeQuery(id+"F2.imprint","IMPRINT",EDGE,{"disambiguationData":[TD([[makeQuery(id+"F2.imprint","INTERSECT",VERTEX,{"derivedFrom":[subQ0,sQuery(id+"F2.wireOp",EDGE,"E31")]}),-1.0]])],"derivedFrom":subQ0})])]})})],"fromTools":[makeQuery(id+"F5.opRevolve","SWEPT_FACE",FACE,{"disambiguationData":[OSD([sQuery(id+"F4.wireOp",EDGE,"E35.right")])]})]}),makeQuery(id+"F12.opExtrude","CAP_FACE",FACE,{"disambiguationData":[OSD([sQuery(id+"F8.wireOp",EDGE,"E38")])],"isStart":false})]});}
            chamfer(context, id + "F13", {"entities" : qUnion([Q0]), "width" : 2.54 * mm, "tangentPropagation" : true});
        }
        {
            var Q0;
            {var subQ1=sQuery(id+"F0.wireOp",EDGE,"E2");var subQ3=sQuery(id+"F0.wireOp",EDGE,"E0");var subQ4=makeQuery(id+"F0.imprint","IMPRINT",EDGE,{"disambiguationData":[TD([[makeQuery(id+"F0.imprint","INTERSECT",VERTEX,{"derivedFrom":[subQ3,subQ1]}),1.0]])],"derivedFrom":subQ3});var subQ7=sQuery(id+"F0.wireOp",EDGE,"E3");var subQ8=makeQuery(id+"F0.imprint","IMPRINT",EDGE,{"disambiguationData":[TD([[makeQuery(id+"F0.imprint","INTERSECT",VERTEX,{"derivedFrom":[subQ3,subQ7]}),-1.0]])],"derivedFrom":subQ3});Q0=makeQuery(id+"F9.boolean.opBoolean","SPLIT",EDGE,{"disambiguationData":[TD([makeQuery(id+"F6.opExtrude","SWEPT_FACE",FACE,{"disambiguationData":[OSD([subQ1])]})])],"derivedFrom":makeQuery(id+"F6.boolean.opBoolean","MERGE",EDGE,{"derivedFrom":[makeQuery(id+"F1.opExtrude","CAP_EDGE",EDGE,{"disambiguationData":[OSD([subQ3])],"isStart":false}),makeQuery(id+"F6.opExtrude","CAP_EDGE",EDGE,{"disambiguationData":[OSD([subQ3]),TDD([subQ4])],"isStart":false}),makeQuery(id+"F6.opExtrude","CAP_EDGE",EDGE,{"disambiguationData":[OSD([subQ3]),TDD([subQ8])],"isStart":false})]})});}
            var Q1;
            {var subQ1=sQuery(id+"F0.wireOp",EDGE,"E2");var subQ3=sQuery(id+"F0.wireOp",EDGE,"E0");var subQ4=makeQuery(id+"F0.imprint","IMPRINT",EDGE,{"disambiguationData":[TD([[makeQuery(id+"F0.imprint","INTERSECT",VERTEX,{"derivedFrom":[subQ3,subQ1]}),1.0]])],"derivedFrom":subQ3});var subQ7=sQuery(id+"F0.wireOp",EDGE,"E3");var subQ8=makeQuery(id+"F0.imprint","IMPRINT",EDGE,{"disambiguationData":[TD([[makeQuery(id+"F0.imprint","INTERSECT",VERTEX,{"derivedFrom":[subQ3,subQ7]}),-1.0]])],"derivedFrom":subQ3});Q1=makeQuery(id+"F9.boolean.opBoolean","SPLIT",EDGE,{"disambiguationData":[TD([makeQuery(id+"F6.opExtrude","SWEPT_FACE",FACE,{"disambiguationData":[OSD([subQ7])]})])],"derivedFrom":makeQuery(id+"F6.boolean.opBoolean","MERGE",EDGE,{"derivedFrom":[makeQuery(id+"F1.opExtrude","CAP_EDGE",EDGE,{"disambiguationData":[OSD([subQ3])],"isStart":false}),makeQuery(id+"F6.opExtrude","CAP_EDGE",EDGE,{"disambiguationData":[OSD([subQ3]),TDD([subQ4])],"isStart":false}),makeQuery(id+"F6.opExtrude","CAP_EDGE",EDGE,{"disambiguationData":[OSD([subQ3]),TDD([subQ8])],"isStart":false})]})});}
            var Q2;
            {var subQ1=sQuery(id+"F0.wireOp",EDGE,"E3");var subQ2=sQuery(id+"F0.wireOp",EDGE,"E1");var subQ5=sQuery(id+"F0.wireOp",EDGE,"E2");var subQ7=makeQuery(id+"F0.imprint","IMPRINT",EDGE,{"disambiguationData":[TD([[makeQuery(id+"F0.imprint","INTERSECT",VERTEX,{"derivedFrom":[subQ2,subQ5]}),1.0]])],"derivedFrom":subQ2});var subQ8=makeQuery(id+"F0.imprint","IMPRINT",EDGE,{"disambiguationData":[TD([[makeQuery(id+"F0.imprint","INTERSECT",VERTEX,{"derivedFrom":[subQ2,subQ1]}),-1.0]])],"derivedFrom":subQ2});Q2=makeQuery(id+"F10.boolean.opBoolean","SPLIT",EDGE,{"disambiguationData":[TD([makeQuery(id+"F6.opExtrude","SWEPT_FACE",FACE,{"disambiguationData":[OSD([subQ1])]})])],"derivedFrom":makeQuery(id+"F6.boolean.opBoolean","MERGE",EDGE,{"derivedFrom":[makeQuery(id+"F1.opExtrude","CAP_EDGE",EDGE,{"disambiguationData":[OSD([subQ2])],"isStart":false}),makeQuery(id+"F6.opExtrude","CAP_EDGE",EDGE,{"disambiguationData":[OSD([subQ2]),TDD([subQ7])],"isStart":false}),makeQuery(id+"F6.opExtrude","CAP_EDGE",EDGE,{"disambiguationData":[OSD([subQ2]),TDD([subQ8])],"isStart":false})]})});}
            var Q3;
            {var subQ1=sQuery(id+"F0.wireOp",EDGE,"E3");var subQ2=sQuery(id+"F0.wireOp",EDGE,"E1");var subQ5=sQuery(id+"F0.wireOp",EDGE,"E2");var subQ7=makeQuery(id+"F0.imprint","IMPRINT",EDGE,{"disambiguationData":[TD([[makeQuery(id+"F0.imprint","INTERSECT",VERTEX,{"derivedFrom":[subQ2,subQ5]}),1.0]])],"derivedFrom":subQ2});var subQ8=makeQuery(id+"F0.imprint","IMPRINT",EDGE,{"disambiguationData":[TD([[makeQuery(id+"F0.imprint","INTERSECT",VERTEX,{"derivedFrom":[subQ2,subQ1]}),-1.0]])],"derivedFrom":subQ2});Q3=makeQuery(id+"F10.boolean.opBoolean","SPLIT",EDGE,{"disambiguationData":[TD([makeQuery(id+"F6.opExtrude","SWEPT_FACE",FACE,{"disambiguationData":[OSD([subQ5])]})])],"derivedFrom":makeQuery(id+"F6.boolean.opBoolean","MERGE",EDGE,{"derivedFrom":[makeQuery(id+"F1.opExtrude","CAP_EDGE",EDGE,{"disambiguationData":[OSD([subQ2])],"isStart":false}),makeQuery(id+"F6.opExtrude","CAP_EDGE",EDGE,{"disambiguationData":[OSD([subQ2]),TDD([subQ7])],"isStart":false}),makeQuery(id+"F6.opExtrude","CAP_EDGE",EDGE,{"disambiguationData":[OSD([subQ2]),TDD([subQ8])],"isStart":false})]})});}
            fillet(context, id + "F14", {"entities" : qUnion([Q0, Q1, Q2, Q3]), "radius" : 3.17 * mm, "tangentPropagation" : true, "allowEdgeOverflow" : false});
        }
        {
            var Q0;
            Q0=makeQuery(id+"F6.opExtrude","SWEPT_EDGE",EDGE,{"disambiguationData":[OSD([sQuery(id+"F0.wireOp",EDGE,"E0"),sQuery(id+"F0.wireOp",EDGE,"E2")])]});
            var Q1;
            Q1=makeQuery(id+"F6.opExtrude","SWEPT_EDGE",EDGE,{"disambiguationData":[OSD([sQuery(id+"F0.wireOp",EDGE,"E1"),sQuery(id+"F0.wireOp",EDGE,"E2")])]});
            var Q2;
            Q2=makeQuery(id+"F6.opExtrude","SWEPT_EDGE",EDGE,{"disambiguationData":[OSD([sQuery(id+"F0.wireOp",EDGE,"E0"),sQuery(id+"F0.wireOp",EDGE,"E3")])]});
            var Q3;
            Q3=makeQuery(id+"F6.opExtrude","SWEPT_EDGE",EDGE,{"disambiguationData":[OSD([sQuery(id+"F0.wireOp",EDGE,"E1"),sQuery(id+"F0.wireOp",EDGE,"E3")])]});
            fillet(context, id + "F15", {"entities" : qUnion([Q0, Q1, Q2, Q3]), "radius" : 3.17 * mm, "tangentPropagation" : true, "allowEdgeOverflow" : false});
        }
        {
            var Q0;
            {var subQ4=sQuery(id+"F0.wireOp",EDGE,"E2");var subQ11=makeQuery(id+"F6.opExtrude","CAP_EDGE",EDGE,{"disambiguationData":[OSD([subQ4])],"isStart":false});Q0=makeQuery(id+"F8.imprint","IMPRINT",FACE,{"disambiguationData":[TD([[makeQuery(id+"F8.imprint","IMPRINT",EDGE,{"derivedFrom":subQ11}),-1.0]])]});}
            var sketch = newSketch(context, id + "F16", { "sketchPlane" : qUnion([Q0])});
            skLineSegment(sketch, "E39", {"start": v(0, 0) * mm, "end": v(-61.96, 0) * mm});
            skLineSegment(sketch, "E40", {"start": v(0, 0) * mm, "end": v(-37.04, 37.04) * mm});
            skCircle(sketch, "E41", {"center": v(-37.04, 37.04) * mm, "radius": 5.72 * mm});
            skLineSegment(sketch, "E42", {"start": v(-37.04, 37.04) * mm, "end": v(-41.08, 33) * mm});
            skLineSegment(sketch, "E43", {"start": v(-37.04, 37.04) * mm, "end": v(-33, 41.08) * mm});
            skLineSegment(sketch, "E44", {"start": v(-33, 41.08) * mm, "end": v(-23.12, 31.2) * mm});
            skLineSegment(sketch, "E45", {"start": v(-41.08, 33) * mm, "end": v(-31.57, 23.49) * mm});
            skLineSegment(sketch, "E46", {"start": v(-31.57, 23.49) * mm, "end": v(-23.12, 31.2) * mm});
            skLineSegment(sketch, "E47", {"start": v(-31.57, 23.49) * mm, "end": v(-30.66, 22.5) * mm});
            skLineSegment(sketch, "E48", {"start": v(-30.66, 22.5) * mm, "end": v(-29.73, 23.76) * mm});
            skLineSegment(sketch, "E49", {"start": v(-29.73, 23.76) * mm, "end": v(-28.39, 25.34) * mm});
            skLineSegment(sketch, "E50", {"start": v(-28.39, 25.34) * mm, "end": v(-27.3, 26.43) * mm});
            skLineSegment(sketch, "E51", {"start": v(-27.3, 26.43) * mm, "end": v(-25.41, 28.31) * mm});
            skLineSegment(sketch, "E52", {"start": v(-25.41, 28.31) * mm, "end": v(-23.97, 29.59) * mm});
            skLineSegment(sketch, "E53", {"start": v(-23.97, 29.59) * mm, "end": v(-22.6, 30.72) * mm});
            skLineSegment(sketch, "E54", {"start": v(-22.6, 30.72) * mm, "end": v(-23.12, 31.2) * mm});
            skSolve(sketch);
        }
        {
            var Q0;
            {var subQ0=sQuery(id+"F16.wireOp",EDGE,"E42");Q0=makeQuery(id+"F16.imprint","IMPRINT",FACE,{"disambiguationData":[TD([[makeQuery(id+"F16.imprint","IMPRINT",EDGE,{"derivedFrom":subQ0}),1.0]])]});}
            var Q1;
            {var subQ0=sQuery(id+"F16.wireOp",EDGE,"E42");Q1=makeQuery(id+"F16.imprint","IMPRINT",FACE,{"disambiguationData":[TD([[makeQuery(id+"F16.imprint","IMPRINT",EDGE,{"derivedFrom":subQ0}),-1.0]])]});}
            var Q2;
            {var subQ0=sQuery(id+"F16.wireOp",EDGE,"E43");Q2=makeQuery(id+"F16.imprint","IMPRINT",FACE,{"disambiguationData":[TD([[makeQuery(id+"F16.imprint","IMPRINT",EDGE,{"derivedFrom":subQ0}),-1.0]])]});}
            var Q3;
            {var subQ0=sQuery(id+"F16.wireOp",EDGE,"E41");var subQ1=sQuery(id+"F16.wireOp",EDGE,"E40");var subQ2=makeQuery(id+"F16.imprint","INTERSECT",VERTEX,{"derivedFrom":[subQ1,subQ0]});Q3=makeQuery(id+"F16.imprint","IMPRINT",FACE,{"disambiguationData":[TD([[makeQuery(id+"F16.imprint","IMPRINT",EDGE,{"disambiguationData":[TD([[subQ2,-1.0]])],"derivedFrom":subQ0}),-1.0]])]});}
            var Q4;
            {var subQ0=sQuery(id+"F16.wireOp",EDGE,"E41");var subQ1=sQuery(id+"F16.wireOp",EDGE,"E40");var subQ2=makeQuery(id+"F16.imprint","INTERSECT",VERTEX,{"derivedFrom":[subQ1,subQ0]});Q4=makeQuery(id+"F16.imprint","IMPRINT",FACE,{"disambiguationData":[TD([[makeQuery(id+"F16.imprint","IMPRINT",EDGE,{"disambiguationData":[TD([[subQ2,1.0]])],"derivedFrom":subQ0}),-1.0]])]});}
            var Q5;
            {var subQ0=sQuery(id+"F16.wireOp",EDGE,"E46");var subQ8=sQuery(id+"F16.wireOp",EDGE,"E45");var subQ9=makeQuery(id+"F16.imprint","INTERSECT",VERTEX,{"derivedFrom":[subQ8,subQ0]});Q5=makeQuery(id+"F16.imprint","IMPRINT",FACE,{"disambiguationData":[TD([[makeQuery(id+"F16.imprint","IMPRINT",EDGE,{"disambiguationData":[TD([[subQ9,-1.0]])],"derivedFrom":subQ0}),1.0]])]});}
            var Q6;
            {var subQ0=sQuery(id+"F16.wireOp",EDGE,"E46");var subQ8=sQuery(id+"F16.wireOp",EDGE,"E44");var subQ9=makeQuery(id+"F16.imprint","INTERSECT",VERTEX,{"derivedFrom":[subQ8,subQ0]});Q6=makeQuery(id+"F16.imprint","IMPRINT",FACE,{"disambiguationData":[TD([[makeQuery(id+"F16.imprint","IMPRINT",EDGE,{"disambiguationData":[TD([[subQ9,1.0]])],"derivedFrom":subQ0}),1.0]])]});}
            var Q7;
            {var subQ0=sQuery(id+"F16.wireOp",EDGE,"E47");Q7=makeQuery(id+"F16.imprint","IMPRINT",FACE,{"disambiguationData":[TD([[makeQuery(id+"F16.imprint","IMPRINT",EDGE,{"derivedFrom":subQ0}),1.0]])]});}
            var Q8;
            {var subQ0=sQuery(id+"F16.wireOp",EDGE,"E52");Q8=makeQuery(id+"F16.imprint","IMPRINT",FACE,{"disambiguationData":[TD([[makeQuery(id+"F16.imprint","IMPRINT",EDGE,{"derivedFrom":subQ0}),1.0]])]});}
            extrude(context, id + "F17", {"entities" : qUnion([Q0, Q1, Q2, Q3, Q4, Q5, Q6, Q7, Q8]), "operationType" : NewBodyOperationType.ADD, "oppositeDirection" : true, "depth" : 15.24 * mm, "offsetDistance" : 25.4 * mm});
        }
        {
            var Q0;
            {var subQ0=sQuery(id+"F16.wireOp",EDGE,"E42");Q0=makeQuery(id+"F16.imprint","IMPRINT",FACE,{"disambiguationData":[TD([[makeQuery(id+"F16.imprint","IMPRINT",EDGE,{"derivedFrom":subQ0}),-1.0]])]});}
            var Q1;
            {var subQ0=sQuery(id+"F16.wireOp",EDGE,"E42");Q1=makeQuery(id+"F16.imprint","IMPRINT",FACE,{"disambiguationData":[TD([[makeQuery(id+"F16.imprint","IMPRINT",EDGE,{"derivedFrom":subQ0}),1.0]])]});}
            var Q2;
            {var subQ0=sQuery(id+"F16.wireOp",EDGE,"E43");Q2=makeQuery(id+"F16.imprint","IMPRINT",FACE,{"disambiguationData":[TD([[makeQuery(id+"F16.imprint","IMPRINT",EDGE,{"derivedFrom":subQ0}),-1.0]])]});}
            extrude(context, id + "F18", {"entities" : qUnion([Q0, Q1, Q2]), "operationType" : NewBodyOperationType.ADD, "depth" : 76.2 * mm, "offsetDistance" : 25.4 * mm});
        }
        {
            var Q0;
            Q0=qCreatedBy(makeId("Right.planeOp"),FACE);
            cPlane(context, id + "F19", {"entities" : qUnion([Q0]), "cplaneType" : CPlaneType.OFFSET, "offset" : 15.24 * mm, "width" : 152.4 * mm, "height" : 152.4 * mm});
        }
        {
            var Q0;
            Q0=qCreatedBy(id+"F19.planeOp",FACE);
            var sketch = newSketch(context, id + "F20", { "sketchPlane" : qUnion([Q0])});
            skLineSegment(sketch, "E55", {"start": v(24.53, 40.83) * mm, "end": v(62.38, 40.83) * mm});
            skLineSegment(sketch, "E56", {"start": v(62.38, 40.83) * mm, "end": v(54.95, 38.88) * mm});
            skLineSegment(sketch, "E57", {"start": v(54.95, 38.88) * mm, "end": v(54.95, 19.53) * mm});
            skLineSegment(sketch, "E58", {"start": v(54.95, 19.53) * mm, "end": v(24.53, 40.83) * mm});
            skSolve(sketch);
        }
        {
            var Q0;
            Q0=makeQuery(id+"F20.imprint","IMPRINT",FACE,{"disambiguationData":[TD([[makeQuery(id+"F20.imprint","IMPRINT",EDGE,{"derivedFrom":sQuery(id+"F20.wireOp",EDGE,"E55")}),-1.0]])]});
            extrude(context, id + "F21", {"entities" : qUnion([Q0]), "operationType" : NewBodyOperationType.REMOVE, "oppositeDirection" : true, "depth" : 30.48 * mm, "offsetDistance" : 25.4 * mm});
        }
        {
            var Q0;
            Q0=qCreatedBy(makeId("Right.planeOp"),FACE);
            cPlane(context, id + "F22", {"entities" : qUnion([Q0]), "cplaneType" : CPlaneType.OFFSET, "offset" : 49.28 * mm, "oppositeDirection" : true, "width" : 152.4 * mm, "height" : 152.4 * mm});
        }
        {
            var Q0;
            Q0=qCreatedBy(id+"F22.planeOp",FACE);
            var sketch = newSketch(context, id + "F23", { "sketchPlane" : qUnion([Q0])});
            skLineSegment(sketch, "E59", {"start": v(37.08, 94.48) * mm, "end": v(39.11, 94.48) * mm});
            skLineSegment(sketch, "E60", {"start": v(39.11, 94.48) * mm, "end": v(39.11, 83.55) * mm});
            skLineSegment(sketch, "E61", {"start": v(39.11, 83.55) * mm, "end": v(39.11, 60.18) * mm});
            skLineSegment(sketch, "E62", {"start": v(39.11, 60.18) * mm, "end": v(39.11, 41.17) * mm});
            skLineSegment(sketch, "E63", {"start": v(39.11, 41.17) * mm, "end": v(35.05, 41.17) * mm});
            skLineSegment(sketch, "E64", {"start": v(35.05, 41.17) * mm, "end": v(35.05, 94.48) * mm});
            skLineSegment(sketch, "E65", {"start": v(35.05, 94.48) * mm, "end": v(37.08, 94.48) * mm});
            skSolve(sketch);
        }
        {
            var Q0;
            Q0=makeQuery(id+"F23.imprint","IMPRINT",FACE,{"disambiguationData":[TD([[makeQuery(id+"F23.imprint","IMPRINT",EDGE,{"derivedFrom":sQuery(id+"F23.wireOp",EDGE,"E59")}),-1.0]])]});
            extrude(context, id + "F24", {"entities" : qUnion([Q0]), "operationType" : NewBodyOperationType.REMOVE, "depth" : 11.43 * mm, "offsetDistance" : 25.4 * mm});
        }
        {
            var Q0;
            Q0=makeQuery(id+"F21.boolean.opBoolean","COPY",FACE,{"derivedFrom":makeQuery(id+"F21.opExtrude","SWEPT_FACE",FACE,{"disambiguationData":[OSD([sQuery(id+"F20.wireOp",EDGE,"E58")])]})});
            var sketch = newSketch(context, id + "F25", { "sketchPlane" : qUnion([Q0])});
            skEllipse(sketch, "E66", {"center": v(0, 17.12) * mm, "majorRadius": 15.44 * mm, "minorRadius": 12.74 * mm, "majorAxis": v(0, 1)});
            skSolve(sketch);
        }
        {
            var Q0;
            {var subQ1=makeQuery(id+"F21.opExtrude","SWEPT_FACE",FACE,{"disambiguationData":[OSD([sQuery(id+"F20.wireOp",EDGE,"E58")])]});var subQ6=sQuery(id+"F8.wireOp",EDGE,"E38");Q0=makeQuery(id+"F25.imprint","IMPRINT",FACE,{"disambiguationData":[TD([[makeQuery(id+"F25.imprint","IMPRINT",EDGE,{"derivedFrom":makeQuery(id+"F21.boolean.opBoolean","INTERSECT",EDGE,{"derivedFrom":[makeQuery(id+"F12.boolean.opBoolean","MERGE",FACE,{"derivedFrom":[makeQuery(id+"F10.boolean.opBoolean","MERGE",FACE,{"derivedFrom":[makeQuery(id+"F9.opExtrude","SWEPT_FACE",FACE,{"disambiguationData":[OSD([subQ6])]}),makeQuery(id+"F10.opExtrude","SWEPT_FACE",FACE,{"disambiguationData":[OSD([subQ6])]})]})],"fromTools":[makeQuery(id+"F12.opExtrude","SWEPT_FACE",FACE,{"disambiguationData":[OSD([subQ6])]})]}),subQ1]})}),1.0]])]});}
            cPlane(context, id + "F26", {"entities" : qUnion([Q0]), "cplaneType" : CPlaneType.OFFSET, "offset" : 12.7 * mm, "width" : 152.4 * mm, "height" : 152.4 * mm});
        }
        {
            var Q0;
            Q0=qCreatedBy(id+"F26.planeOp",FACE);
            var sketch = newSketch(context, id + "F27", { "sketchPlane" : qUnion([Q0])});
            skCircle(sketch, "E67", {"center": v(0, 15.54) * mm, "radius": 14.35 * mm});
            skSolve(sketch);
        }
        {
            var Q1;
            Q1 = qSketchRegion(id + "F25", true);
            var Q2;
            Q2=makeQuery(id+"F27.imprint","IMPRINT",FACE,{"disambiguationData":[TD([[makeQuery(id+"F27.imprint","IMPRINT",EDGE,{"derivedFrom":sQuery(id+"F27.wireOp",EDGE,"E67")}),1.0]])]});
            loft(context, id + "F28", {"operationType" : NewBodyOperationType.ADD, "sheetProfilesArray" : [{ "sheetProfileEntities" : qUnion([Q1]) }, { "sheetProfileEntities" : qUnion([Q2]) }]});
        }
        {
            var Q0;
            Q0=makeQuery(id+"F28.opLoft","CAP_FACE",FACE,{"disambiguationData":[OSD([makeQuery(id+"F27.imprint","IMPRINT",FACE,{"disambiguationData":[TD([[makeQuery(id+"F27.imprint","IMPRINT",EDGE,{"derivedFrom":sQuery(id+"F27.wireOp",EDGE,"E67")}),1.0]])]})])],"isStart":true});
            extrude(context, id + "F29", {"entities" : qUnion([Q0]), "operationType" : NewBodyOperationType.ADD, "depth" : 31.75 * mm, "offsetDistance" : 25.4 * mm});
        }
        {
            var Q0;
            Q0=makeQuery(id+"F29.opExtrude","CAP_FACE",FACE,{"disambiguationData":[OSD([makeQuery(id+"F27.imprint","IMPRINT",FACE,{"disambiguationData":[TD([[makeQuery(id+"F27.imprint","IMPRINT",EDGE,{"derivedFrom":sQuery(id+"F27.wireOp",EDGE,"E67")}),1.0]])]})])],"isStart":false});
            var sketch = newSketch(context, id + "F30", { "sketchPlane" : qUnion([Q0])});
            skLineSegment(sketch, "E68", {"start": v(9.66, 4.93) * mm, "end": v(-9.66, 26.15) * mm, "construction": true});
            skLineSegment(sketch, "E69", {"start": v(-9.66, 26.15) * mm, "end": v(10.61, 25.2) * mm, "construction": true});
            skLineSegment(sketch, "E70", {"start": v(10.61, 25.2) * mm, "end": v(-10.61, 5.88) * mm, "construction": true});
            skLineSegment(sketch, "E71", {"start": v(-10.61, 5.88) * mm, "end": v(9.66, 4.93) * mm, "construction": true});
            skCircle(sketch, "E72", {"center": v(0, 15.54) * mm, "radius": 10.8 * mm});
            skSolve(sketch);
        }
        {
            var Q0;
            Q0=makeQuery(id+"F30.imprint","IMPRINT",FACE,{"disambiguationData":[TD([[makeQuery(id+"F30.imprint","IMPRINT",EDGE,{"derivedFrom":sQuery(id+"F30.wireOp",EDGE,"E72")}),1.0]])]});
            extrude(context, id + "F31", {"entities" : qUnion([Q0]), "operationType" : NewBodyOperationType.REMOVE, "oppositeDirection" : true, "depth" : 45.14 * mm, "offsetDistance" : 25.4 * mm});
        }
        {
            var Q0;
            {var subQ0=sQuery(id+"F8.wireOp",EDGE,"E38");Q0=makeQuery(id+"F31.boolean.opBoolean","INTERSECT",EDGE,{"derivedFrom":[makeQuery(id+"F12.boolean.opBoolean","MERGE",FACE,{"derivedFrom":[makeQuery(id+"F10.boolean.opBoolean","MERGE",FACE,{"derivedFrom":[makeQuery(id+"F9.opExtrude","SWEPT_FACE",FACE,{"disambiguationData":[OSD([subQ0])]}),makeQuery(id+"F10.opExtrude","SWEPT_FACE",FACE,{"disambiguationData":[OSD([subQ0])]})]})],"fromTools":[makeQuery(id+"F12.opExtrude","SWEPT_FACE",FACE,{"disambiguationData":[OSD([subQ0])]})]}),makeQuery(id+"F31.opExtrude","CAP_FACE",FACE,{"disambiguationData":[OSD([sQuery(id+"F30.wireOp",EDGE,"E72")])],"isStart":false})]});}
            chamfer(context, id + "F32", {"entities" : qUnion([Q0]), "width" : 2.54 * mm, "tangentPropagation" : true});
        }
    });
